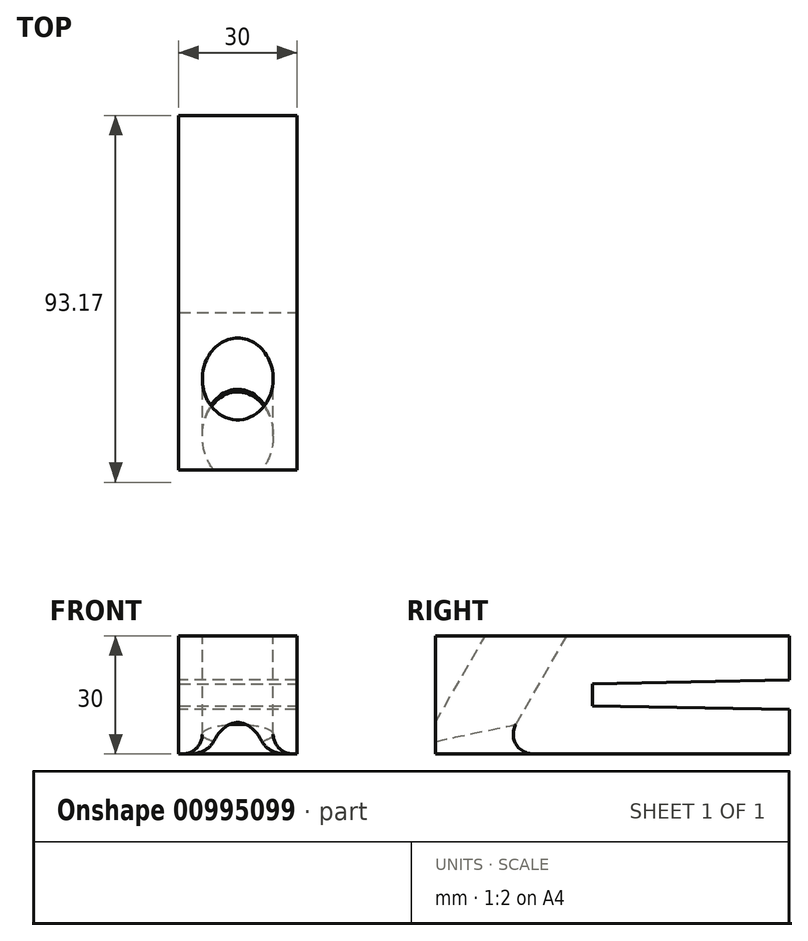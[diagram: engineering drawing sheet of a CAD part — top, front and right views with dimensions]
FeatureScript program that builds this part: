
annotation { "Feature Type Name" : "Feature", "Feature Type Description" : "" }
export const myFeature = defineFeature(function(context is Context, id is Id, definition is map)
    precondition{}
    {
        {
            var Q0;
            Q0=qCreatedBy(makeId("Front.planeOp"),FACE);
            var sketch = newSketch(context, id + "F0", { "sketchPlane" : qUnion([Q0])});
            skLineSegment(sketch, "E0.bottom", {"start": v(0, 0) * mm, "end": v(30, 0) * mm});
            skLineSegment(sketch, "E0.top", {"start": v(0, 30) * mm, "end": v(30, 30) * mm});
            skLineSegment(sketch, "E0.left", {"start": v(0, 0) * mm, "end": v(0, 30) * mm});
            skLineSegment(sketch, "E0.right", {"start": v(30, 0) * mm, "end": v(30, 30) * mm});
            skSolve(sketch);
        }
        {
            var Q0;
            Q0 = qSketchRegion(id + "F0", true);
            extrude(context, id + "F1", {"entities" : qUnion([Q0]), "depth" : 40 * mm, "offsetDistance" : 25 * mm});
        }
        {
            var Q0;
            Q0=makeQuery(id+"F1.opExtrude","CAP_FACE",FACE,{"disambiguationData":[OSD([sQuery(id+"F0.wireOp",EDGE,"E0.bottom"),sQuery(id+"F0.wireOp",EDGE,"E0.top"),sQuery(id+"F0.wireOp",EDGE,"E0.left"),sQuery(id+"F0.wireOp",EDGE,"E0.right")])],"isStart":true});
            var sketch = newSketch(context, id + "F2", { "sketchPlane" : qUnion([Q0])});
            skLineSegment(sketch, "E1.bottom", {"start": v(0, 0) * mm, "end": v(-30, 0) * mm});
            skLineSegment(sketch, "E1.top", {"start": v(0, 12.25) * mm, "end": v(-30, 12.25) * mm});
            skLineSegment(sketch, "E1.left", {"start": v(0, 0) * mm, "end": v(0, 12.25) * mm});
            skLineSegment(sketch, "E1.right", {"start": v(-30, 0) * mm, "end": v(-30, 12.25) * mm});
            skLineSegment(sketch, "E2.bottom", {"start": v(0, 30) * mm, "end": v(-30, 30) * mm});
            skLineSegment(sketch, "E2.top", {"start": v(0, 17.75) * mm, "end": v(-30, 17.75) * mm});
            skLineSegment(sketch, "E2.left", {"start": v(0, 30) * mm, "end": v(0, 17.75) * mm});
            skLineSegment(sketch, "E2.right", {"start": v(-30, 30) * mm, "end": v(-30, 17.75) * mm});
            skLineSegment(sketch, "E3", {"start": v(0, 12.25) * mm, "end": v(0, 17.75) * mm});
            skSolve(sketch);
        }
        {
            var Q0;
            Q0 = qSketchRegion(id + "F2", true);
            extrude(context, id + "F3", {"entities" : qUnion([Q0]), "operationType" : NewBodyOperationType.ADD, "depth" : 50 * mm, "offsetDistance" : 25 * mm});
        }
        {
            var Q0;
            Q0=makeQuery(id+"F3.boolean.opBoolean","MERGE",FACE,{"derivedFrom":[makeQuery(id+"F1.opExtrude","SWEPT_FACE",FACE,{"disambiguationData":[OSD([sQuery(id+"F0.wireOp",EDGE,"E0.left")])]}),makeQuery(id+"F3.opExtrude","SWEPT_FACE",FACE,{"disambiguationData":[OSD([sQuery(id+"F2.wireOp",EDGE,"E1.left")])]}),makeQuery(id+"F3.opExtrude","SWEPT_FACE",FACE,{"disambiguationData":[OSD([sQuery(id+"F2.wireOp",EDGE,"E2.left")])]})]});
            var sketch = newSketch(context, id + "F4", { "sketchPlane" : qUnion([Q0])});
            skLineSegment(sketch, "E4", {"start": v(0, 17.75) * mm, "end": v(-50, 18.75) * mm});
            skLineSegment(sketch, "E5", {"start": v(-50, 18.75) * mm, "end": v(-50, 17.75) * mm});
            skLineSegment(sketch, "E6", {"start": v(-50, 17.75) * mm, "end": v(0, 17.75) * mm});
            skLineSegment(sketch, "E7", {"start": v(0, 12.25) * mm, "end": v(-50, 11.25) * mm});
            skLineSegment(sketch, "E8", {"start": v(-50, 11.25) * mm, "end": v(-50, 12.25) * mm});
            skLineSegment(sketch, "E9", {"start": v(-50, 12.25) * mm, "end": v(0, 12.25) * mm});
            skSolve(sketch);
        }
        {
            var Q0;
            Q0 = qSketchRegion(id + "F4", true);
            extrude(context, id + "F5", {"entities" : qUnion([Q0]), "operationType" : NewBodyOperationType.REMOVE, "endBound" : BoundingType.UP_TO_NEXT, "oppositeDirection" : true, "depth" : 25 * mm, "offsetDistance" : 25 * mm});
        }
        {
            var Q0;
            Q0=makeQuery(id+"F1.opExtrude","CAP_EDGE",EDGE,{"disambiguationData":[OSD([sQuery(id+"F0.wireOp",EDGE,"E0.bottom")])],"isStart":false});
            cPlane(context, id + "F6", {"entities" : qUnion([Q0]), "cplaneType" : CPlaneType.LINE_ANGLE, "offset" : 25 * mm, "angle" : 60 * degree, "width" : 150 * mm, "height" : 150 * mm});
        }
        {
            var Q0;
            Q0=qCreatedBy(id+"F6.planeOp",FACE);
            cPlane(context, id + "F7", {"entities" : qUnion([Q0]), "cplaneType" : CPlaneType.OFFSET, "offset" : 30.9 * mm, "width" : 150 * mm, "height" : 150 * mm});
        }
        {
            var Q0;
            Q0=qCreatedBy(id+"F7.planeOp",FACE);
            var sketch = newSketch(context, id + "F8", { "sketchPlane" : qUnion([Q0])});
            skCircle(sketch, "E10", {"center": v(15, -29.64) * mm, "radius": 9 * mm});
            skSolve(sketch);
        }
        {
            var Q0;
            Q0 = qSketchRegion(id + "F8", true);
            extrude(context, id + "F9", {"entities" : qUnion([Q0]), "operationType" : NewBodyOperationType.REMOVE, "endBound" : BoundingType.THROUGH_ALL, "oppositeDirection" : true, "depth" : 25 * mm, "offsetDistance" : 25 * mm, "hasSecondDirection" : true, "secondDirectionOppositeDirection" : false, "secondDirectionDepth" : 25 * mm});
        }
        {
            var Q0;
            Q0=makeQuery(id+"F9.boolean.opBoolean","INTERSECT",EDGE,{"derivedFrom":[makeQuery(id+"F3.boolean.opBoolean","MERGE",FACE,{"derivedFrom":[makeQuery(id+"F1.opExtrude","SWEPT_FACE",FACE,{"disambiguationData":[OSD([sQuery(id+"F0.wireOp",EDGE,"E0.bottom")])]}),makeQuery(id+"F3.opExtrude","SWEPT_FACE",FACE,{"disambiguationData":[OSD([sQuery(id+"F2.wireOp",EDGE,"E1.bottom")])]})]}),makeQuery(id+"F9.opExtrude","SWEPT_FACE",FACE,{"disambiguationData":[OSD([sQuery(id+"F8.wireOp",EDGE,"E10")])]})]});
            fillet(context, id + "F10", {"entities" : qUnion([Q0]), "radius" : 5 * mm, "tangentPropagation" : true, "allowEdgeOverflow" : false});
        }
    });
